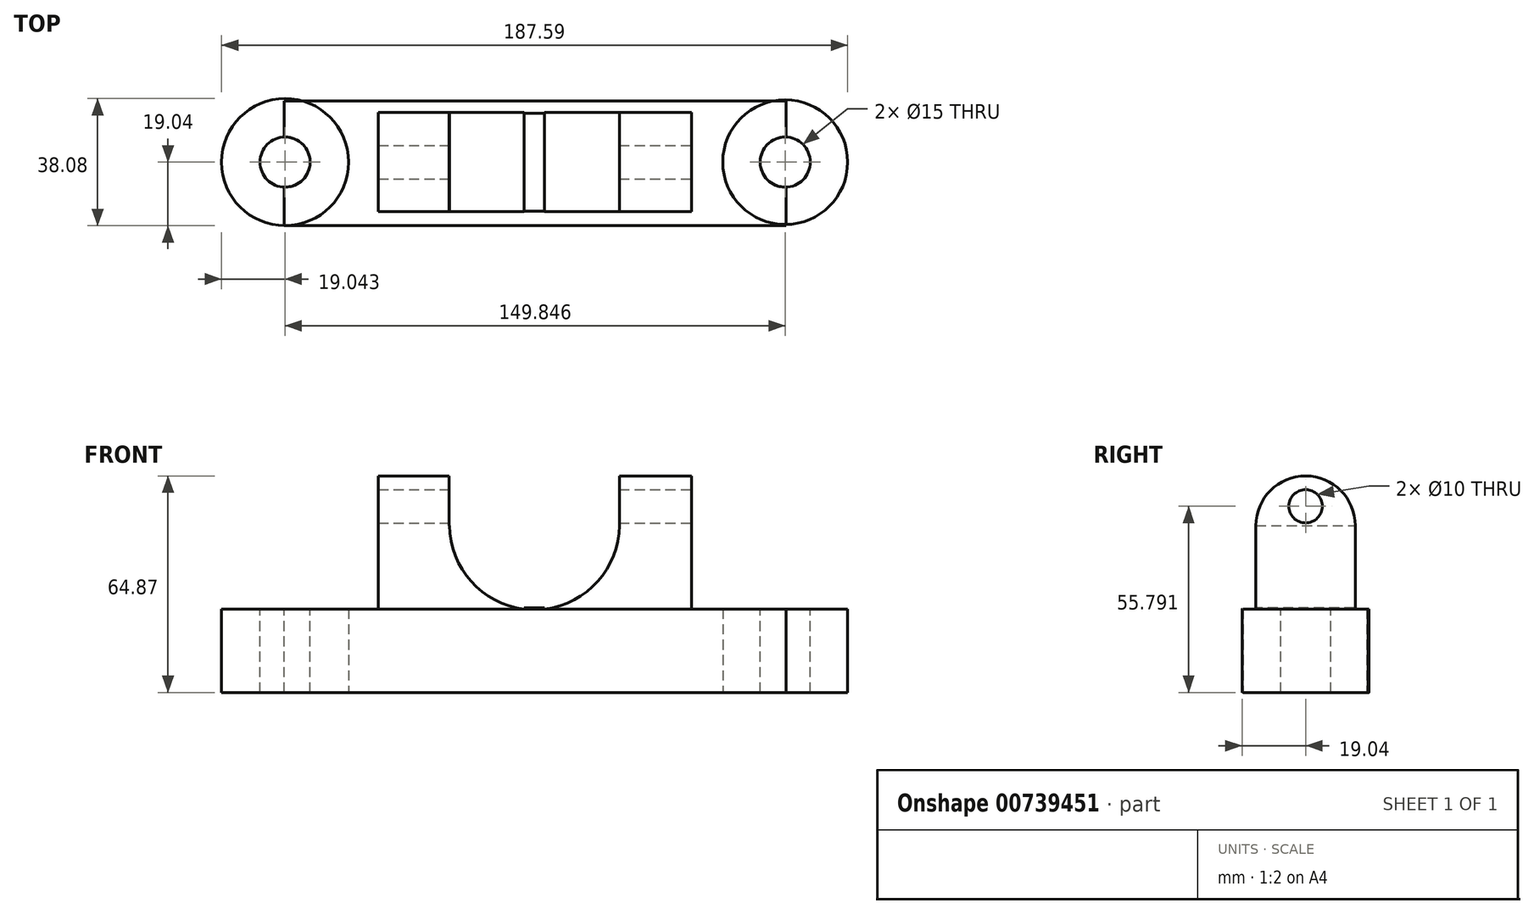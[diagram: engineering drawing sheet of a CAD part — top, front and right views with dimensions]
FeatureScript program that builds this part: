
annotation { "Feature Type Name" : "Feature", "Feature Type Description" : "" }
export const myFeature = defineFeature(function(context is Context, id is Id, definition is map)
    precondition{}
    {
        {
            var Q0;
            Q0=qCreatedBy(makeId("Top.planeOp"),FACE);
            var sketch = newSketch(context, id + "F0", { "sketchPlane" : qUnion([Q0])});
            skCircle(sketch, "E0", {"center": v(-74.86, 0) * mm, "radius": 19.04 * mm});
            skSolve(sketch);
        }
        {
            var Q0;
            Q0=qCreatedBy(makeId("Top.planeOp"),FACE);
            var sketch = newSketch(context, id + "F1", { "sketchPlane" : qUnion([Q0])});
            skCircle(sketch, "E1", {"center": v(74.99, 0) * mm, "radius": 18.7 * mm});
            skSolve(sketch);
        }
        {
            var Q0;
            Q0=makeQuery(id+"F0.imprint","IMPRINT",FACE,{"disambiguationData":[TD([[makeQuery(id+"F0.imprint","IMPRINT",EDGE,{"derivedFrom":sQuery(id+"F0.wireOp",EDGE,"E0")}),1.0]])]});
            var Q1;
            Q1=makeQuery(id+"F1.imprint","IMPRINT",FACE,{"disambiguationData":[TD([[makeQuery(id+"F1.imprint","IMPRINT",EDGE,{"derivedFrom":sQuery(id+"F1.wireOp",EDGE,"E1")}),1.0]])]});
            extrude(context, id + "F2", {"entities" : qUnion([Q0, Q1]), "depth" : 25 * mm, "offsetDistance" : 25 * mm});
        }
        {
            var Q0;
            Q0=qCreatedBy(makeId("Top.planeOp"),FACE);
            var sketch = newSketch(context, id + "F3", { "sketchPlane" : qUnion([Q0])});
            skLineSegment(sketch, "E2.bottom", {"start": v(-75.15, 18.31) * mm, "end": v(75.27, 18.31) * mm});
            skLineSegment(sketch, "E2.top", {"start": v(-75.15, -19) * mm, "end": v(75.27, -19) * mm});
            skLineSegment(sketch, "E2.left", {"start": v(-75.15, 18.31) * mm, "end": v(-75.15, -19) * mm});
            skLineSegment(sketch, "E2.right", {"start": v(75.27, 18.31) * mm, "end": v(75.27, -19) * mm});
            skSolve(sketch);
        }
        {
            var Q0;
            Q0=makeQuery(id+"F3.imprint","IMPRINT",FACE,{"disambiguationData":[TD([[makeQuery(id+"F3.imprint","IMPRINT",EDGE,{"derivedFrom":sQuery(id+"F3.wireOp",EDGE,"E2.bottom")}),-1.0]])]});
            extrude(context, id + "F4", {"entities" : qUnion([Q0]), "depth" : 25 * mm, "offsetDistance" : 25 * mm});
        }
        {
            var Q0;
            Q0=makeQuery(id+"F2.opExtrude","CAP_FACE",FACE,{"disambiguationData":[OSD([sQuery(id+"F0.wireOp",EDGE,"E0")])],"isStart":false});
            var sketch = newSketch(context, id + "F5", { "sketchPlane" : qUnion([Q0])});
            skPoint(sketch, "E3", {"position": v(-74.86, 0) * mm});
            skSolve(sketch);
        }
        {
            var Q0;
            Q0=sQuery(id+"F5.wireOp",VERTEX,"E3");
            var Q1;
            Q1=makeQuery(id+"F2.opExtrude","SWEPT_BODY",BODY,{"disambiguationData":[OSD([sQuery(id+"F0.wireOp",EDGE,"E0")])]});
            var Q2;
            Q2=makeQuery(id+"F4.opExtrude","SWEPT_BODY",BODY,{"disambiguationData":[OSD([sQuery(id+"F3.wireOp",EDGE,"E2.bottom"),sQuery(id+"F3.wireOp",EDGE,"E2.top"),sQuery(id+"F3.wireOp",EDGE,"E2.left"),sQuery(id+"F3.wireOp",EDGE,"E2.right")])]});
            hole(context, id + "F6", {"style" : HoleStyle.SIMPLE, "endStyle" : HoleEndStyle.THROUGH, "holeDiameter" : 15 * mm, "majorDiameter" : 5 * mm, "isTappedThrough" : true, "tappedDepth" : 12 * mm, "tapClearance" : 3, "locations" : qUnion([Q0]), "scope" : qUnion([Q1, Q2])});
        }
        {
            var Q0;
            Q0=makeQuery(id+"F2.opExtrude","CAP_FACE",FACE,{"disambiguationData":[OSD([sQuery(id+"F1.wireOp",EDGE,"E1")])],"isStart":false});
            var sketch = newSketch(context, id + "F7", { "sketchPlane" : qUnion([Q0])});
            skPoint(sketch, "E4", {"position": v(74.99, 0) * mm});
            skSolve(sketch);
        }
        {
            var Q0;
            Q0=sQuery(id+"F7.wireOp",VERTEX,"E4");
            var Q1;
            Q1=makeQuery(id+"F4.opExtrude","SWEPT_BODY",BODY,{"disambiguationData":[OSD([sQuery(id+"F3.wireOp",EDGE,"E2.bottom"),sQuery(id+"F3.wireOp",EDGE,"E2.top"),sQuery(id+"F3.wireOp",EDGE,"E2.left"),sQuery(id+"F3.wireOp",EDGE,"E2.right")])]});
            var Q2;
            Q2=makeQuery(id+"F2.opExtrude","SWEPT_BODY",BODY,{"disambiguationData":[OSD([sQuery(id+"F1.wireOp",EDGE,"E1")])]});
            hole(context, id + "F8", {"style" : HoleStyle.SIMPLE, "endStyle" : HoleEndStyle.THROUGH, "holeDiameter" : 15 * mm, "majorDiameter" : 5 * mm, "isTappedThrough" : true, "tappedDepth" : 12 * mm, "tapClearance" : 3, "locations" : qUnion([Q0]), "scope" : qUnion([Q1, Q2])});
        }
        {
            var Q0;
            Q0=makeQuery(id+"F4.opExtrude","CAP_FACE",FACE,{"disambiguationData":[OSD([sQuery(id+"F3.wireOp",EDGE,"E2.bottom"),sQuery(id+"F3.wireOp",EDGE,"E2.top"),sQuery(id+"F3.wireOp",EDGE,"E2.left"),sQuery(id+"F3.wireOp",EDGE,"E2.right")])],"isStart":false});
            var sketch = newSketch(context, id + "F9", { "sketchPlane" : qUnion([Q0])});
            skPoint(sketch, "E5", {"position": v(0, 0) * mm});
            skSolve(sketch);
        }
        {
            var Q0;
            {var subQ3=sQuery(id+"F3.wireOp",EDGE,"E2.bottom");Q0=makeQuery(id+"F9.imprint","IMPRINT",FACE,{"disambiguationData":[TD([[makeQuery(id+"F9.imprint","IMPRINT",EDGE,{"derivedFrom":makeQuery(id+"F4.opExtrude","CAP_EDGE",EDGE,{"disambiguationData":[OSD([subQ3])],"isStart":false})}),-1.0]])]});}
            var sketch = newSketch(context, id + "F10", { "sketchPlane" : qUnion([Q0])});
            skLineSegment(sketch, "E6.bottom", {"start": v(46.9, -14.87) * mm, "end": v(-46.9, -14.87) * mm});
            skLineSegment(sketch, "E6.top", {"start": v(46.9, 14.87) * mm, "end": v(-46.9, 14.87) * mm});
            skLineSegment(sketch, "E6.left", {"start": v(46.9, -14.87) * mm, "end": v(46.9, 14.87) * mm});
            skLineSegment(sketch, "E6.right", {"start": v(-46.9, -14.87) * mm, "end": v(-46.9, 14.87) * mm});
            skPoint(sketch, "E6.middle", {"position": v(0, 0) * mm});
            skSolve(sketch);
        }
        {
            var Q0;
            Q0=makeQuery(id+"F10.imprint","IMPRINT",FACE,{"disambiguationData":[TD([[makeQuery(id+"F10.imprint","IMPRINT",EDGE,{"derivedFrom":sQuery(id+"F10.wireOp",EDGE,"E6.bottom")}),-1.0]])]});
            extrude(context, id + "F11", {"entities" : qUnion([Q0]), "operationType" : NewBodyOperationType.ADD, "depth" : 25 * mm, "offsetDistance" : 25 * mm});
        }
        {
            var Q0;
            Q0=makeQuery(id+"F11.opExtrude","SWEPT_FACE",FACE,{"disambiguationData":[OSD([sQuery(id+"F10.wireOp",EDGE,"E6.left")])]});
            var sketch = newSketch(context, id + "F12", { "sketchPlane" : qUnion([Q0])});
            skArc(sketch, "E7", {"start": v(14.87, 50) * mm, "mid": v(0, 64.87) * mm, "end": v(-14.87, 50) * mm});
            skSolve(sketch);
        }
        {
            var Q0;
            Q0=makeQuery(id+"F11.opExtrude","SWEPT_FACE",FACE,{"disambiguationData":[OSD([sQuery(id+"F10.wireOp",EDGE,"E6.right")])]});
            var sketch = newSketch(context, id + "F13", { "sketchPlane" : qUnion([Q0])});
            skArc(sketch, "E8", {"start": v(14.87, 50) * mm, "mid": v(0, 64.87) * mm, "end": v(-14.87, 50) * mm});
            skSolve(sketch);
        }
        {
            var Q0;
            Q0=makeQuery(id+"F12.imprint","IMPRINT",FACE,{"disambiguationData":[TD([[makeQuery(id+"F12.imprint","IMPRINT",EDGE,{"derivedFrom":sQuery(id+"F12.wireOp",EDGE,"E7")}),1.0]])]});
            extrude(context, id + "F14", {"entities" : qUnion([Q0]), "operationType" : NewBodyOperationType.ADD, "oppositeDirection" : true, "depth" : 21.6 * mm, "offsetDistance" : 25 * mm});
        }
        {
            var Q0;
            Q0=makeQuery(id+"F11.opExtrude","SWEPT_FACE",FACE,{"disambiguationData":[OSD([sQuery(id+"F10.wireOp",EDGE,"E6.bottom")])]});
            var sketch = newSketch(context, id + "F15", { "sketchPlane" : qUnion([Q0])});
            skArc(sketch, "E9", {"start": v(-25.6, 50) * mm, "mid": v(-0.15, 24.82) * mm, "end": v(25.3, 50) * mm});
            skSolve(sketch);
        }
        {
            var Q0;
            {var subQ0=sQuery(id+"F15.wireOp",EDGE,"E9");var subQ1=sQuery(id+"F10.wireOp",EDGE,"E6.bottom");var subQ2=makeQuery(id+"F11.opExtrude","CAP_EDGE",EDGE,{"disambiguationData":[OSD([subQ1])],"isStart":false});var subQ3=makeQuery(id+"F14.boolean.opBoolean","SPLIT",EDGE,{"derivedFrom":subQ2});var subQ4=makeQuery(id+"F15.imprint","INTERSECT",VERTEX,{"derivedFrom":[subQ3,subQ0]});Q0=makeQuery(id+"F15.imprint","IMPRINT",FACE,{"disambiguationData":[TD([[makeQuery(id+"F15.imprint","IMPRINT",EDGE,{"disambiguationData":[TD([[subQ4,-1.0]])],"derivedFrom":subQ0}),1.0]])]});}
            extrude(context, id + "F16", {"entities" : qUnion([Q0]), "operationType" : NewBodyOperationType.REMOVE, "endBound" : BoundingType.THROUGH_ALL, "oppositeDirection" : true, "depth" : 76.08 * mm, "offsetDistance" : 25 * mm});
        }
        {
            var Q0;
            Q0=makeQuery(id+"F13.imprint","IMPRINT",FACE,{"disambiguationData":[TD([[makeQuery(id+"F13.imprint","IMPRINT",EDGE,{"derivedFrom":sQuery(id+"F13.wireOp",EDGE,"E8")}),1.0]])]});
            extrude(context, id + "F17", {"entities" : qUnion([Q0]), "operationType" : NewBodyOperationType.ADD, "oppositeDirection" : true, "depth" : 21.23 * mm, "offsetDistance" : 25 * mm});
        }
        {
            var Q0;
            {var subQ0=sQuery(id+"F10.wireOp",EDGE,"E6.left");Q0=makeQuery(id+"F14.boolean.opBoolean","MERGE",FACE,{"derivedFrom":[makeQuery(id+"F11.opExtrude","SWEPT_FACE",FACE,{"disambiguationData":[OSD([subQ0])]}),makeQuery(id+"F14.opExtrude","CAP_FACE",FACE,{"disambiguationData":[OSD([subQ0,sQuery(id+"F12.wireOp",EDGE,"E7")])],"isStart":true})]});}
            var sketch = newSketch(context, id + "F18", { "sketchPlane" : qUnion([Q0])});
            skLineSegment(sketch, "E10", {"start": v(14.87, 50) * mm, "end": v(-14.87, 50) * mm});
            skSolve(sketch);
        }
        {
            var Q0;
            Q0=makeQuery(id+"F18.imprint","IMPRINT",FACE,{"disambiguationData":[TD([[makeQuery(id+"F18.imprint","IMPRINT",EDGE,{"derivedFrom":sQuery(id+"F18.wireOp",EDGE,"E10")}),-1.0]])]});
            var sketch = newSketch(context, id + "F19", { "sketchPlane" : qUnion([Q0])});
            skPoint(sketch, "E11", {"position": v(0, 55.8) * mm});
            skSolve(sketch);
        }
        {
            var Q0;
            Q0=sQuery(id+"F19.wireOp",VERTEX,"E11");
            var Q1;
            Q1=makeQuery(id+"F4.opExtrude","SWEPT_BODY",BODY,{"disambiguationData":[OSD([sQuery(id+"F3.wireOp",EDGE,"E2.bottom"),sQuery(id+"F3.wireOp",EDGE,"E2.top"),sQuery(id+"F3.wireOp",EDGE,"E2.left"),sQuery(id+"F3.wireOp",EDGE,"E2.right")])]});
            hole(context, id + "F20", {"style" : HoleStyle.SIMPLE, "endStyle" : HoleEndStyle.THROUGH, "holeDiameter" : 10 * mm, "majorDiameter" : 5 * mm, "isTappedThrough" : true, "tappedDepth" : 12 * mm, "tapClearance" : 3, "locations" : qUnion([Q0]), "scope" : qUnion([Q1])});
        }
        {
            var Q0;
            {var subQ3=sQuery(id+"F3.wireOp",EDGE,"E2.bottom");Q0=makeQuery(id+"F9.imprint","IMPRINT",FACE,{"disambiguationData":[TD([[makeQuery(id+"F9.imprint","IMPRINT",EDGE,{"derivedFrom":makeQuery(id+"F4.opExtrude","CAP_EDGE",EDGE,{"disambiguationData":[OSD([subQ3])],"isStart":false})}),-1.0]])]});}
            var sketch = newSketch(context, id + "F21", { "sketchPlane" : qUnion([Q0])});
            skLineSegment(sketch, "E12.bottom", {"start": v(-3.2, 14.68) * mm, "end": v(2.9, 14.68) * mm});
            skLineSegment(sketch, "E12.top", {"start": v(-3.2, -14.7) * mm, "end": v(2.9, -14.7) * mm});
            skLineSegment(sketch, "E12.left", {"start": v(-3.2, 14.68) * mm, "end": v(-3.2, -14.7) * mm});
            skLineSegment(sketch, "E12.right", {"start": v(2.9, 14.68) * mm, "end": v(2.9, -14.7) * mm});
            skSolve(sketch);
        }
        {
            var Q0;
            Q0=makeQuery(id+"F21.imprint","IMPRINT",FACE,{"disambiguationData":[TD([[makeQuery(id+"F21.imprint","IMPRINT",EDGE,{"derivedFrom":sQuery(id+"F21.wireOp",EDGE,"E12.bottom")}),-1.0]])]});
            extrude(context, id + "F22", {"entities" : qUnion([Q0]), "operationType" : NewBodyOperationType.ADD, "depth" : 0.3 * mm, "offsetDistance" : 25 * mm});
        }
    });
